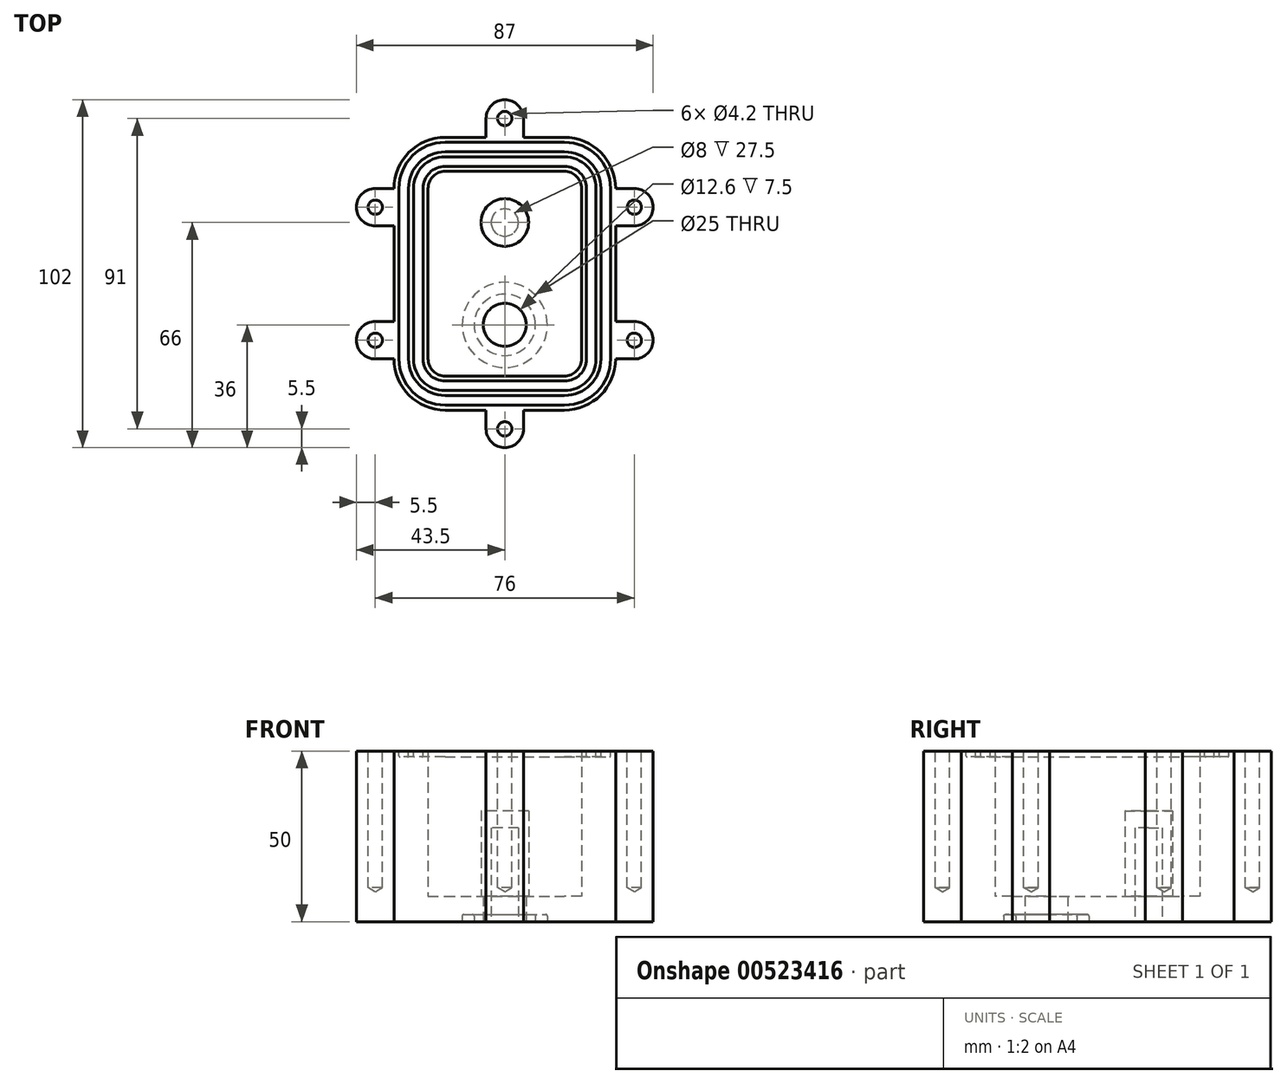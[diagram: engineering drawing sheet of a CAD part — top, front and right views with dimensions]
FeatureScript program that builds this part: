
annotation { "Feature Type Name" : "Feature", "Feature Type Description" : "" }
export const myFeature = defineFeature(function(context is Context, id is Id, definition is map)
    precondition{}
    {
        {
            var Q0;
            Q0=qCreatedBy(makeId("Top.planeOp"),FACE);
            var sketch = newSketch(context, id + "F0", { "sketchPlane" : qUnion([Q0])});
            skLineSegment(sketch, "E0.bottom", {"start": v(-17.5, -30) * mm, "end": v(17.5, -30) * mm});
            skLineSegment(sketch, "E0.top", {"start": v(-17.5, 30) * mm, "end": v(17.5, 30) * mm});
            skLineSegment(sketch, "E0.left", {"start": v(-22.5, -25) * mm, "end": v(-22.5, 25) * mm});
            skLineSegment(sketch, "E0.right", {"start": v(22.5, -25) * mm, "end": v(22.5, 25) * mm});
            skPoint(sketch, "E0.middle", {"position": v(0, 0) * mm});
            skPoint(sketch, "E1.visualSharp", {"position": v(22.5, -30) * mm});
            skArc(sketch, "E1.filletArc", {"start": v(17.5, -30) * mm, "mid": v(21.04, -28.54) * mm, "end": v(22.5, -25) * mm});
            skPoint(sketch, "E2.visualSharp", {"position": v(-22.5, -30) * mm});
            skArc(sketch, "E2.filletArc", {"start": v(-22.5, -25) * mm, "mid": v(-21.04, -28.54) * mm, "end": v(-17.5, -30) * mm});
            skPoint(sketch, "E3.visualSharp", {"position": v(-22.5, 30) * mm});
            skArc(sketch, "E3.filletArc", {"start": v(-17.5, 30) * mm, "mid": v(-21.04, 28.54) * mm, "end": v(-22.5, 25) * mm});
            skPoint(sketch, "E4.visualSharp", {"position": v(22.5, 30) * mm});
            skArc(sketch, "E4.filletArc", {"start": v(22.5, 25) * mm, "mid": v(21.04, 28.54) * mm, "end": v(17.5, 30) * mm});
            skArc(sketch, "E5.0", {"start": v(-32.5, -25) * mm, "mid": v(-28.1, -35.6) * mm, "end": v(-17.5, -40) * mm});
            skLineSegment(sketch, "E5.1", {"start": v(-17.5, -40) * mm, "end": v(-5.5, -40) * mm});
            skLineSegment(sketch, "E5.2", {"start": v(-32.5, -14) * mm, "end": v(-32.5, 14) * mm});
            skArc(sketch, "E5.3", {"start": v(17.5, -40) * mm, "mid": v(28.1, -35.6) * mm, "end": v(32.5, -25) * mm});
            skArc(sketch, "E5.4", {"start": v(-17.5, 40) * mm, "mid": v(-28.1, 35.6) * mm, "end": v(-32.5, 25) * mm});
            skLineSegment(sketch, "E5.5", {"start": v(-17.5, 40) * mm, "end": v(-5.5, 40) * mm});
            skArc(sketch, "E5.6", {"start": v(32.5, 25) * mm, "mid": v(28.1, 35.6) * mm, "end": v(17.5, 40) * mm});
            skLineSegment(sketch, "E5.7", {"start": v(32.5, -14) * mm, "end": v(32.5, 14) * mm});
            skArc(sketch, "E6", {"start": v(-38, 25) * mm, "mid": v(-43.5, 19.5) * mm, "end": v(-38, 14) * mm});
            skLineSegment(sketch, "E7", {"start": v(-38, 25) * mm, "end": v(-32.5, 25) * mm});
            skLineSegment(sketch, "E8", {"start": v(-38, 14) * mm, "end": v(-32.5, 14) * mm});
            skCircle(sketch, "E9", {"center": v(-38, 19.5) * mm, "radius": 2.5 * mm, "construction": true});
            skLineSegment(sketch, "E10", {"start": v(0, 49.94) * mm, "end": v(0, -61.1) * mm, "construction": true});
            skLineSegment(sketch, "E11", {"start": v(-88.08, 0) * mm, "end": v(87.86, 0) * mm, "construction": true});
            skLineSegment(sketch, "E12.MirrorCS", {"start": v(38, 25) * mm, "end": v(32.5, 25) * mm});
            skLineSegment(sketch, "E13.MirrorCS", {"start": v(38, 14) * mm, "end": v(32.5, 14) * mm});
            skArc(sketch, "E14.MirrorCS", {"start": v(38, 25) * mm, "mid": v(43.5, 19.5) * mm, "end": v(38, 14) * mm});
            skCircle(sketch, "E15.MirrorC", {"center": v(38, 19.5) * mm, "radius": 2.5 * mm, "construction": true});
            skLineSegment(sketch, "E16.MirrorCS", {"start": v(-38, -14) * mm, "end": v(-32.5, -14) * mm});
            skLineSegment(sketch, "E17.MirrorCS", {"start": v(-38, -25) * mm, "end": v(-32.5, -25) * mm});
            skArc(sketch, "E18.MirrorCS", {"start": v(-38, -25) * mm, "mid": v(-43.5, -19.5) * mm, "end": v(-38, -14) * mm});
            skCircle(sketch, "E19.MirrorC", {"center": v(-38, -19.5) * mm, "radius": 2.5 * mm, "construction": true});
            skArc(sketch, "E20.MirrorCS", {"start": v(32.5, -25) * mm, "mid": v(28.1, -35.6) * mm, "end": v(17.5, -40) * mm});
            skLineSegment(sketch, "E21.MirrorCS", {"start": v(38, -14) * mm, "end": v(32.5, -14) * mm});
            skArc(sketch, "E22.MirrorCS", {"start": v(38, -25) * mm, "mid": v(43.5, -19.5) * mm, "end": v(38, -14) * mm});
            skLineSegment(sketch, "E23.MirrorCS", {"start": v(32.5, 14) * mm, "end": v(32.5, -14) * mm});
            skCircle(sketch, "E24.MirrorC", {"center": v(38, -19.5) * mm, "radius": 2.5 * mm, "construction": true});
            skLineSegment(sketch, "E25.MirrorCS", {"start": v(38, -25) * mm, "end": v(32.5, -25) * mm});
            skPoint(sketch, "E26.orphan", {"position": v(32.5, 25) * mm});
            skArc(sketch, "E27", {"start": v(5.5, 45.5) * mm, "mid": v(0, 51) * mm, "end": v(-5.5, 45.5) * mm});
            skCircle(sketch, "E28", {"center": v(0, 45.5) * mm, "radius": 2.5 * mm, "construction": true});
            skLineSegment(sketch, "E29", {"start": v(5.5, 45.5) * mm, "end": v(5.5, 40) * mm});
            skLineSegment(sketch, "E30", {"start": v(-5.5, 45.5) * mm, "end": v(-5.5, 40) * mm});
            skLineSegment(sketch, "E31.trimOffspring", {"start": v(5.5, 40) * mm, "end": v(17.5, 40) * mm});
            skArc(sketch, "E32.MirrorCS", {"start": v(5.5, -45.5) * mm, "mid": v(0, -51) * mm, "end": v(-5.5, -45.5) * mm});
            skCircle(sketch, "E33.MirrorC", {"center": v(0, -45.5) * mm, "radius": 2.5 * mm, "construction": true});
            skLineSegment(sketch, "E34.MirrorCS", {"start": v(5.5, -45.5) * mm, "end": v(5.5, -40) * mm});
            skLineSegment(sketch, "E35.MirrorCS", {"start": v(-5.5, -45.5) * mm, "end": v(-5.5, -40) * mm});
            skLineSegment(sketch, "E36.trimOffspring", {"start": v(5.5, -40) * mm, "end": v(17.5, -40) * mm});
            skSolve(sketch);
        }
        {
            var Q0;
            Q0=qSketchRegion(id+"F0",true);
            extrude(context, id + "F1", {"entities" : qUnion([Q0]), "depth" : 50 * mm, "offsetDistance" : 25 * mm});
        }
        {
            var Q0;
            Q0=qCreatedBy(makeId("Top.planeOp"),FACE);
            var sketch = newSketch(context, id + "F2", { "sketchPlane" : qUnion([Q0])});
            skArc(sketch, "E37.0.0", {"start": v(38, 25) * mm, "mid": v(43.5, 19.5) * mm, "end": v(38, 14) * mm});
            skLineSegment(sketch, "E37.0.1", {"start": v(38, 14) * mm, "end": v(32.5, 14) * mm});
            skLineSegment(sketch, "E37.0.2", {"start": v(32.5, 14) * mm, "end": v(32.5, -14) * mm});
            skLineSegment(sketch, "E37.0.3", {"start": v(32.5, -14) * mm, "end": v(38, -14) * mm});
            skArc(sketch, "E37.0.4", {"start": v(38, -14) * mm, "mid": v(43.5, -19.5) * mm, "end": v(38, -25) * mm});
            skLineSegment(sketch, "E37.0.5", {"start": v(38, -25) * mm, "end": v(32.5, -25) * mm});
            skArc(sketch, "E37.0.6", {"start": v(32.5, -25) * mm, "mid": v(28.1, -35.6) * mm, "end": v(17.5, -40) * mm});
            skLineSegment(sketch, "E37.0.7", {"start": v(17.5, -40) * mm, "end": v(5.5, -40) * mm});
            skLineSegment(sketch, "E37.0.8", {"start": v(5.5, -40) * mm, "end": v(5.5, -45.5) * mm});
            skArc(sketch, "E37.0.9", {"start": v(5.5, -45.5) * mm, "mid": v(0, -51) * mm, "end": v(-5.5, -45.5) * mm});
            skLineSegment(sketch, "E37.0.10", {"start": v(-5.5, -45.5) * mm, "end": v(-5.5, -40) * mm});
            skLineSegment(sketch, "E37.0.11", {"start": v(-5.5, -40) * mm, "end": v(-17.5, -40) * mm});
            skArc(sketch, "E37.0.12", {"start": v(-17.5, -40) * mm, "mid": v(-28.1, -35.6) * mm, "end": v(-32.5, -25) * mm});
            skLineSegment(sketch, "E37.0.13", {"start": v(-32.5, -25) * mm, "end": v(-38, -25) * mm});
            skArc(sketch, "E37.0.14", {"start": v(-38, -25) * mm, "mid": v(-43.5, -19.5) * mm, "end": v(-38, -14) * mm});
            skLineSegment(sketch, "E37.0.15", {"start": v(-38, -14) * mm, "end": v(-32.5, -14) * mm});
            skLineSegment(sketch, "E37.0.16", {"start": v(-32.5, -14) * mm, "end": v(-32.5, 14) * mm});
            skLineSegment(sketch, "E37.0.17", {"start": v(-32.5, 14) * mm, "end": v(-38, 14) * mm});
            skArc(sketch, "E37.0.18", {"start": v(-38, 14) * mm, "mid": v(-43.5, 19.5) * mm, "end": v(-38, 25) * mm});
            skLineSegment(sketch, "E37.0.19", {"start": v(-38, 25) * mm, "end": v(-32.5, 25) * mm});
            skArc(sketch, "E37.0.20", {"start": v(-32.5, 25) * mm, "mid": v(-28.1, 35.6) * mm, "end": v(-17.5, 40) * mm});
            skLineSegment(sketch, "E37.0.21", {"start": v(-17.5, 40) * mm, "end": v(-5.5, 40) * mm});
            skLineSegment(sketch, "E37.0.22", {"start": v(-5.5, 40) * mm, "end": v(-5.5, 45.5) * mm});
            skArc(sketch, "E37.0.23", {"start": v(-5.5, 45.5) * mm, "mid": v(0, 51) * mm, "end": v(5.5, 45.5) * mm});
            skLineSegment(sketch, "E37.0.24", {"start": v(5.5, 45.5) * mm, "end": v(5.5, 40) * mm});
            skLineSegment(sketch, "E37.0.25", {"start": v(5.5, 40) * mm, "end": v(17.5, 40) * mm});
            skArc(sketch, "E37.0.26", {"start": v(17.5, 40) * mm, "mid": v(28.1, 35.6) * mm, "end": v(32.5, 25) * mm});
            skLineSegment(sketch, "E37.0.27", {"start": v(32.5, 25) * mm, "end": v(38, 25) * mm});
            skSolve(sketch);
        }
        {
            var Q0;
            Q0=qSketchRegion(id+"F2",true);
            var Q1;
            Q1=qSketchRegion(id+"F0",true);
            extrude(context, id + "F3", {"entities" : qUnion([Q0, Q1]), "operationType" : NewBodyOperationType.ADD, "depth" : 7.5 * mm, "offsetDistance" : 25 * mm});
        }
        {
            var Q0;
            Q0=makeQuery(id+"F1.opExtrude","CAP_FACE",FACE,{"disambiguationData":[OSD([sQuery(id+"F0.wireOp",EDGE,"E0.bottom"),sQuery(id+"F0.wireOp",EDGE,"E0.top"),sQuery(id+"F0.wireOp",EDGE,"E0.left"),sQuery(id+"F0.wireOp",EDGE,"E0.right"),sQuery(id+"F0.wireOp",EDGE,"E1.filletArc"),sQuery(id+"F0.wireOp",EDGE,"E2.filletArc"),sQuery(id+"F0.wireOp",EDGE,"E3.filletArc"),sQuery(id+"F0.wireOp",EDGE,"E4.filletArc"),sQuery(id+"F0.wireOp",EDGE,"E5.0"),sQuery(id+"F0.wireOp",EDGE,"E5.1"),sQuery(id+"F0.wireOp",EDGE,"E5.2"),sQuery(id+"F0.wireOp",EDGE,"E5.3"),sQuery(id+"F0.wireOp",EDGE,"E5.4"),sQuery(id+"F0.wireOp",EDGE,"E5.5"),sQuery(id+"F0.wireOp",EDGE,"E5.6"),sQuery(id+"F0.wireOp",EDGE,"E5.7")])],"isStart":false});
            var sketch = newSketch(context, id + "F4", { "sketchPlane" : qUnion([Q0])});
            skLineSegment(sketch, "E38.0", {"start": v(-17.5, 31.47) * mm, "end": v(17.5, 31.47) * mm});
            skArc(sketch, "E38.1", {"start": v(23.97, 25) * mm, "mid": v(22.07, 29.57) * mm, "end": v(17.5, 31.47) * mm});
            skArc(sketch, "E38.2", {"start": v(-17.5, 31.47) * mm, "mid": v(-22.07, 29.57) * mm, "end": v(-23.97, 25) * mm});
            skLineSegment(sketch, "E38.3", {"start": v(23.97, -25) * mm, "end": v(23.97, 25) * mm});
            skLineSegment(sketch, "E38.4", {"start": v(-23.97, -25) * mm, "end": v(-23.97, 25) * mm});
            skArc(sketch, "E38.5", {"start": v(-23.97, -25) * mm, "mid": v(-22.07, -29.57) * mm, "end": v(-17.5, -31.47) * mm});
            skLineSegment(sketch, "E38.6", {"start": v(-17.5, -31.47) * mm, "end": v(17.5, -31.47) * mm});
            skArc(sketch, "E38.7", {"start": v(17.5, -31.47) * mm, "mid": v(22.07, -29.57) * mm, "end": v(23.97, -25) * mm});
            skLineSegment(sketch, "E39.0", {"start": v(-17.5, 34.27) * mm, "end": v(17.5, 34.27) * mm});
            skArc(sketch, "E39.1", {"start": v(26.77, 25) * mm, "mid": v(24.05, 31.55) * mm, "end": v(17.5, 34.27) * mm});
            skArc(sketch, "E39.2", {"start": v(-17.5, 34.27) * mm, "mid": v(-24.05, 31.55) * mm, "end": v(-26.77, 25) * mm});
            skLineSegment(sketch, "E39.3", {"start": v(26.77, -25) * mm, "end": v(26.77, 25) * mm});
            skLineSegment(sketch, "E39.4", {"start": v(-26.77, -25) * mm, "end": v(-26.77, 25) * mm});
            skArc(sketch, "E39.5", {"start": v(-26.77, -25) * mm, "mid": v(-24.05, -31.55) * mm, "end": v(-17.5, -34.27) * mm});
            skLineSegment(sketch, "E39.6", {"start": v(-17.5, -34.27) * mm, "end": v(17.5, -34.27) * mm});
            skArc(sketch, "E39.7", {"start": v(17.5, -34.27) * mm, "mid": v(24.05, -31.55) * mm, "end": v(26.77, -25) * mm});
            skLineSegment(sketch, "E40.0", {"start": v(-17.5, 35.73) * mm, "end": v(17.5, 35.73) * mm});
            skArc(sketch, "E40.1", {"start": v(28.23, 25) * mm, "mid": v(25.09, 32.59) * mm, "end": v(17.5, 35.73) * mm});
            skArc(sketch, "E40.2", {"start": v(-17.5, 35.73) * mm, "mid": v(-25.09, 32.59) * mm, "end": v(-28.23, 25) * mm});
            skLineSegment(sketch, "E40.3", {"start": v(28.23, -25) * mm, "end": v(28.23, 25) * mm});
            skLineSegment(sketch, "E40.4", {"start": v(-28.23, -25) * mm, "end": v(-28.23, 25) * mm});
            skArc(sketch, "E40.5", {"start": v(-28.23, -25) * mm, "mid": v(-25.09, -32.59) * mm, "end": v(-17.5, -35.73) * mm});
            skLineSegment(sketch, "E40.6", {"start": v(-17.5, -35.73) * mm, "end": v(17.5, -35.73) * mm});
            skArc(sketch, "E40.7", {"start": v(17.5, -35.73) * mm, "mid": v(25.09, -32.59) * mm, "end": v(28.23, -25) * mm});
            skLineSegment(sketch, "E41.0", {"start": v(-17.5, 38.53) * mm, "end": v(17.5, 38.53) * mm});
            skArc(sketch, "E41.1", {"start": v(31.03, 25) * mm, "mid": v(27.07, 34.57) * mm, "end": v(17.5, 38.53) * mm});
            skArc(sketch, "E41.2", {"start": v(-17.5, 38.53) * mm, "mid": v(-27.07, 34.57) * mm, "end": v(-31.03, 25) * mm});
            skLineSegment(sketch, "E41.3", {"start": v(31.03, -25) * mm, "end": v(31.03, 25) * mm});
            skLineSegment(sketch, "E41.4", {"start": v(-31.03, -25) * mm, "end": v(-31.03, 25) * mm});
            skArc(sketch, "E41.5", {"start": v(-31.03, -25) * mm, "mid": v(-27.07, -34.57) * mm, "end": v(-17.5, -38.53) * mm});
            skLineSegment(sketch, "E41.6", {"start": v(-17.5, -38.53) * mm, "end": v(17.5, -38.53) * mm});
            skArc(sketch, "E41.7", {"start": v(17.5, -38.53) * mm, "mid": v(27.07, -34.57) * mm, "end": v(31.03, -25) * mm});
            skLineSegment(sketch, "E42", {"start": v(0, 30) * mm, "end": v(0, 31.47) * mm, "construction": true});
            skLineSegment(sketch, "E43", {"start": v(0, 31.47) * mm, "end": v(0, 34.27) * mm, "construction": true});
            skLineSegment(sketch, "E44", {"start": v(0, 34.27) * mm, "end": v(0, 35.73) * mm, "construction": true});
            skLineSegment(sketch, "E45", {"start": v(0, 35.73) * mm, "end": v(0, 38.53) * mm, "construction": true});
            skLineSegment(sketch, "E46", {"start": v(0, 38.53) * mm, "end": v(0, 40) * mm, "construction": true});
            skSolve(sketch);
        }
        {
            var Q0;
            Q0=makeQuery(id+"F4.imprint","IMPRINT",FACE,{"disambiguationData":[TD([[makeQuery(id+"F4.imprint","IMPRINT",EDGE,{"derivedFrom":sQuery(id+"F4.wireOp",EDGE,"E40.0")}),1.0]])]});
            var Q1;
            Q1=makeQuery(id+"F4.imprint","IMPRINT",FACE,{"disambiguationData":[TD([[makeQuery(id+"F4.imprint","IMPRINT",EDGE,{"derivedFrom":sQuery(id+"F4.wireOp",EDGE,"E38.0")}),1.0]])]});
            extrude(context, id + "F5", {"entities" : qUnion([Q0, Q1]), "operationType" : NewBodyOperationType.REMOVE, "oppositeDirection" : true, "depth" : 1.7 * mm, "offsetDistance" : 25 * mm});
        }
        {
            var Q0;
            {var subQ0=sQuery(id+"F0.wireOp",EDGE,"E25.MirrorCS");var subQ1=sQuery(id+"F0.wireOp",EDGE,"E23.MirrorCS");var subQ2=sQuery(id+"F0.wireOp",EDGE,"E22.MirrorCS");var subQ3=sQuery(id+"F0.wireOp",EDGE,"E21.MirrorCS");var subQ4=sQuery(id+"F0.wireOp",EDGE,"E20.MirrorCS");var subQ5=sQuery(id+"F0.wireOp",EDGE,"E18.MirrorCS");var subQ6=sQuery(id+"F0.wireOp",EDGE,"E17.MirrorCS");var subQ7=sQuery(id+"F0.wireOp",EDGE,"E16.MirrorCS");var subQ8=sQuery(id+"F0.wireOp",EDGE,"E14.MirrorCS");var subQ9=sQuery(id+"F0.wireOp",EDGE,"E13.MirrorCS");var subQ10=sQuery(id+"F0.wireOp",EDGE,"E5.4");var subQ11=sQuery(id+"F0.wireOp",EDGE,"E5.2");var subQ12=sQuery(id+"F0.wireOp",EDGE,"E5.1");var subQ13=sQuery(id+"F0.wireOp",EDGE,"E5.0");var subQ14=sQuery(id+"F0.wireOp",EDGE,"E5.5");var subQ15=sQuery(id+"F0.wireOp",EDGE,"E5.6");var subQ16=sQuery(id+"F0.wireOp",EDGE,"E6");var subQ17=sQuery(id+"F0.wireOp",EDGE,"E7");var subQ18=sQuery(id+"F0.wireOp",EDGE,"E8");var subQ19=sQuery(id+"F0.wireOp",EDGE,"E12.MirrorCS");Q0=makeQuery(id+"F5.boolean.opBoolean","SPLIT",FACE,{"disambiguationData":[TD([makeQuery(id+"F1.opExtrude","SWEPT_FACE",FACE,{"disambiguationData":[OSD([subQ13])]})])],"derivedFrom":makeQuery(id+"F1.opExtrude","CAP_FACE",FACE,{"disambiguationData":[OSD([sQuery(id+"F0.wireOp",EDGE,"E0.bottom"),sQuery(id+"F0.wireOp",EDGE,"E0.top"),sQuery(id+"F0.wireOp",EDGE,"E0.left"),sQuery(id+"F0.wireOp",EDGE,"E0.right"),sQuery(id+"F0.wireOp",EDGE,"E1.filletArc"),sQuery(id+"F0.wireOp",EDGE,"E2.filletArc"),sQuery(id+"F0.wireOp",EDGE,"E3.filletArc"),sQuery(id+"F0.wireOp",EDGE,"E4.filletArc"),subQ13,subQ12,subQ11,subQ10,subQ14,subQ15,subQ16,subQ17,subQ18,subQ19,subQ9,subQ8,subQ7,subQ6,subQ5,subQ4,subQ3,subQ2,subQ1,subQ0])],"isStart":false})});}
            var sketch = newSketch(context, id + "F6", { "sketchPlane" : qUnion([Q0])});
            skPoint(sketch, "E47", {"position": v(-38, 19.5) * mm});
            skPoint(sketch, "E48", {"position": v(0, 45.5) * mm});
            skPoint(sketch, "E49", {"position": v(38, 19.5) * mm});
            skPoint(sketch, "E50", {"position": v(38, -19.5) * mm});
            skPoint(sketch, "E51", {"position": v(0, -45.5) * mm});
            skPoint(sketch, "E52", {"position": v(-38, -19.5) * mm});
            skSolve(sketch);
        }
        {
            var Q0;
            Q0=sQuery(id+"F6.wireOp",VERTEX,"E47");
            var Q1;
            Q1=sQuery(id+"F6.wireOp",VERTEX,"E48");
            var Q2;
            Q2=sQuery(id+"F6.wireOp",VERTEX,"E49");
            var Q3;
            Q3=sQuery(id+"F6.wireOp",VERTEX,"E50");
            var Q4;
            Q4=sQuery(id+"F6.wireOp",VERTEX,"E51");
            var Q5;
            Q5=sQuery(id+"F6.wireOp",VERTEX,"E52");
            var Q6;
            Q6=makeQuery(id+"F1.opExtrude","SWEPT_BODY",BODY,{"disambiguationData":[OSD([sQuery(id+"F0.wireOp",EDGE,"E0.bottom"),sQuery(id+"F0.wireOp",EDGE,"E0.top"),sQuery(id+"F0.wireOp",EDGE,"E0.left"),sQuery(id+"F0.wireOp",EDGE,"E0.right"),sQuery(id+"F0.wireOp",EDGE,"E1.filletArc"),sQuery(id+"F0.wireOp",EDGE,"E2.filletArc"),sQuery(id+"F0.wireOp",EDGE,"E3.filletArc"),sQuery(id+"F0.wireOp",EDGE,"E4.filletArc"),sQuery(id+"F0.wireOp",EDGE,"E5.0"),sQuery(id+"F0.wireOp",EDGE,"E5.1"),sQuery(id+"F0.wireOp",EDGE,"E5.2"),sQuery(id+"F0.wireOp",EDGE,"E5.4"),sQuery(id+"F0.wireOp",EDGE,"E5.5"),sQuery(id+"F0.wireOp",EDGE,"E5.6"),sQuery(id+"F0.wireOp",EDGE,"E6"),sQuery(id+"F0.wireOp",EDGE,"E7"),sQuery(id+"F0.wireOp",EDGE,"E8"),sQuery(id+"F0.wireOp",EDGE,"E12.MirrorCS"),sQuery(id+"F0.wireOp",EDGE,"E13.MirrorCS"),sQuery(id+"F0.wireOp",EDGE,"E14.MirrorCS"),sQuery(id+"F0.wireOp",EDGE,"E16.MirrorCS"),sQuery(id+"F0.wireOp",EDGE,"E17.MirrorCS"),sQuery(id+"F0.wireOp",EDGE,"E18.MirrorCS"),sQuery(id+"F0.wireOp",EDGE,"E20.MirrorCS"),sQuery(id+"F0.wireOp",EDGE,"E21.MirrorCS"),sQuery(id+"F0.wireOp",EDGE,"E22.MirrorCS"),sQuery(id+"F0.wireOp",EDGE,"E23.MirrorCS"),sQuery(id+"F0.wireOp",EDGE,"E25.MirrorCS"),sQuery(id+"F0.wireOp",EDGE,"E27"),sQuery(id+"F0.wireOp",EDGE,"E29"),sQuery(id+"F0.wireOp",EDGE,"E30"),sQuery(id+"F0.wireOp",EDGE,"E31.trimOffspring"),sQuery(id+"F0.wireOp",EDGE,"E32.MirrorCS"),sQuery(id+"F0.wireOp",EDGE,"E34.MirrorCS"),sQuery(id+"F0.wireOp",EDGE,"E35.MirrorCS"),sQuery(id+"F0.wireOp",EDGE,"E36.trimOffspring")])]});
            hole(context, id + "F7", {"style" : HoleStyle.SIMPLE, "endStyle" : HoleEndStyle.BLIND, "standardTappedOrClearance" : lookupTablePath({ "standard" : "ISO", "engagement" : "75%", "pitch" : "0.8 mm", "size" : "M5", "type" : "Tapped" }), "standardBlindInLast" : lookupTablePath({ "standard" : "ISO", "engagement" : "75%", "pitch" : "0.8 mm", "size" : "M5", "type" : "Tapped" }), "holeDiameter" : 4.2 * mm, "showTappedDepth" : true, "holeDepth" : 40 * mm, "isTappedThrough" : true, "tappedDepth" : 37.6 * mm, "tapClearance" : 3, "locations" : qUnion([Q0, Q1, Q2, Q3, Q4, Q5]), "scope" : qUnion([Q6]), "majorDiameter" : 5 * mm});
        }
        {
            var Q0;
            Q0=makeQuery(id+"F5.boolean.opBoolean","COPY",FACE,{"derivedFrom":makeQuery(id+"F5.opExtrude","CAP_FACE",FACE,{"disambiguationData":[OSD([sQuery(id+"F4.wireOp",EDGE,"E40.0"),sQuery(id+"F4.wireOp",EDGE,"E40.1"),sQuery(id+"F4.wireOp",EDGE,"E40.2"),sQuery(id+"F4.wireOp",EDGE,"E40.3"),sQuery(id+"F4.wireOp",EDGE,"E40.4"),sQuery(id+"F4.wireOp",EDGE,"E40.5"),sQuery(id+"F4.wireOp",EDGE,"E40.6"),sQuery(id+"F4.wireOp",EDGE,"E40.7"),sQuery(id+"F4.wireOp",EDGE,"E41.0"),sQuery(id+"F4.wireOp",EDGE,"E41.1"),sQuery(id+"F4.wireOp",EDGE,"E41.2"),sQuery(id+"F4.wireOp",EDGE,"E41.3"),sQuery(id+"F4.wireOp",EDGE,"E41.4"),sQuery(id+"F4.wireOp",EDGE,"E41.5"),sQuery(id+"F4.wireOp",EDGE,"E41.6"),sQuery(id+"F4.wireOp",EDGE,"E41.7")])],"isStart":false})});
            var Q1;
            Q1=makeQuery(id+"F5.boolean.opBoolean","COPY",FACE,{"derivedFrom":makeQuery(id+"F5.opExtrude","CAP_FACE",FACE,{"disambiguationData":[OSD([sQuery(id+"F4.wireOp",EDGE,"E38.0"),sQuery(id+"F4.wireOp",EDGE,"E38.1"),sQuery(id+"F4.wireOp",EDGE,"E38.2"),sQuery(id+"F4.wireOp",EDGE,"E38.3"),sQuery(id+"F4.wireOp",EDGE,"E38.4"),sQuery(id+"F4.wireOp",EDGE,"E38.5"),sQuery(id+"F4.wireOp",EDGE,"E38.6"),sQuery(id+"F4.wireOp",EDGE,"E38.7"),sQuery(id+"F4.wireOp",EDGE,"E39.0"),sQuery(id+"F4.wireOp",EDGE,"E39.1"),sQuery(id+"F4.wireOp",EDGE,"E39.2"),sQuery(id+"F4.wireOp",EDGE,"E39.3"),sQuery(id+"F4.wireOp",EDGE,"E39.4"),sQuery(id+"F4.wireOp",EDGE,"E39.5"),sQuery(id+"F4.wireOp",EDGE,"E39.6"),sQuery(id+"F4.wireOp",EDGE,"E39.7")])],"isStart":false})});
            fillet(context, id + "F8", {"entities" : qUnion([Q0, Q1]), "radius" : 0.3 * mm, "tangentPropagation" : true, "allowEdgeOverflow" : false});
        }
        {
            var Q0;
            Q0=makeQuery(id+"F3.boolean.opBoolean","MERGE",FACE,{"derivedFrom":[makeQuery(id+"F3.opExtrude","CAP_FACE",FACE,{"disambiguationData":[OSD([sQuery(id+"F0.wireOp",EDGE,"E0.bottom"),sQuery(id+"F0.wireOp",EDGE,"E0.top"),sQuery(id+"F0.wireOp",EDGE,"E0.left"),sQuery(id+"F0.wireOp",EDGE,"E0.right"),sQuery(id+"F0.wireOp",EDGE,"E1.filletArc"),sQuery(id+"F0.wireOp",EDGE,"E2.filletArc"),sQuery(id+"F0.wireOp",EDGE,"E3.filletArc"),sQuery(id+"F0.wireOp",EDGE,"E4.filletArc"),sQuery(id+"F0.wireOp",EDGE,"E5.0"),sQuery(id+"F0.wireOp",EDGE,"E5.1"),sQuery(id+"F0.wireOp",EDGE,"E5.2"),sQuery(id+"F0.wireOp",EDGE,"E5.4"),sQuery(id+"F0.wireOp",EDGE,"E5.5"),sQuery(id+"F0.wireOp",EDGE,"E5.6"),sQuery(id+"F0.wireOp",EDGE,"E6"),sQuery(id+"F0.wireOp",EDGE,"E7"),sQuery(id+"F0.wireOp",EDGE,"E8"),sQuery(id+"F0.wireOp",EDGE,"E12.MirrorCS"),sQuery(id+"F0.wireOp",EDGE,"E13.MirrorCS"),sQuery(id+"F0.wireOp",EDGE,"E14.MirrorCS"),sQuery(id+"F0.wireOp",EDGE,"E16.MirrorCS"),sQuery(id+"F0.wireOp",EDGE,"E17.MirrorCS"),sQuery(id+"F0.wireOp",EDGE,"E18.MirrorCS"),sQuery(id+"F0.wireOp",EDGE,"E20.MirrorCS"),sQuery(id+"F0.wireOp",EDGE,"E21.MirrorCS"),sQuery(id+"F0.wireOp",EDGE,"E22.MirrorCS"),sQuery(id+"F0.wireOp",EDGE,"E23.MirrorCS"),sQuery(id+"F0.wireOp",EDGE,"E25.MirrorCS"),sQuery(id+"F0.wireOp",EDGE,"E27"),sQuery(id+"F0.wireOp",EDGE,"E29"),sQuery(id+"F0.wireOp",EDGE,"E30"),sQuery(id+"F0.wireOp",EDGE,"E31.trimOffspring"),sQuery(id+"F0.wireOp",EDGE,"E32.MirrorCS"),sQuery(id+"F0.wireOp",EDGE,"E34.MirrorCS"),sQuery(id+"F0.wireOp",EDGE,"E35.MirrorCS"),sQuery(id+"F0.wireOp",EDGE,"E36.trimOffspring")])],"isStart":false}),makeQuery(id+"F3.opExtrude","CAP_FACE",FACE,{"disambiguationData":[OSD([sQuery(id+"F2.wireOp",EDGE,"E37.0.0"),sQuery(id+"F2.wireOp",EDGE,"E37.0.1"),sQuery(id+"F2.wireOp",EDGE,"E37.0.2"),sQuery(id+"F2.wireOp",EDGE,"E37.0.3"),sQuery(id+"F2.wireOp",EDGE,"E37.0.4"),sQuery(id+"F2.wireOp",EDGE,"E37.0.5"),sQuery(id+"F2.wireOp",EDGE,"E37.0.6"),sQuery(id+"F2.wireOp",EDGE,"E37.0.7"),sQuery(id+"F2.wireOp",EDGE,"E37.0.8"),sQuery(id+"F2.wireOp",EDGE,"E37.0.9"),sQuery(id+"F2.wireOp",EDGE,"E37.0.10"),sQuery(id+"F2.wireOp",EDGE,"E37.0.11"),sQuery(id+"F2.wireOp",EDGE,"E37.0.12"),sQuery(id+"F2.wireOp",EDGE,"E37.0.13"),sQuery(id+"F2.wireOp",EDGE,"E37.0.14"),sQuery(id+"F2.wireOp",EDGE,"E37.0.15"),sQuery(id+"F2.wireOp",EDGE,"E37.0.16"),sQuery(id+"F2.wireOp",EDGE,"E37.0.17"),sQuery(id+"F2.wireOp",EDGE,"E37.0.18"),sQuery(id+"F2.wireOp",EDGE,"E37.0.19"),sQuery(id+"F2.wireOp",EDGE,"E37.0.20"),sQuery(id+"F2.wireOp",EDGE,"E37.0.21"),sQuery(id+"F2.wireOp",EDGE,"E37.0.22"),sQuery(id+"F2.wireOp",EDGE,"E37.0.23"),sQuery(id+"F2.wireOp",EDGE,"E37.0.24"),sQuery(id+"F2.wireOp",EDGE,"E37.0.25"),sQuery(id+"F2.wireOp",EDGE,"E37.0.26"),sQuery(id+"F2.wireOp",EDGE,"E37.0.27")])],"isStart":false})]});
            var sketch = newSketch(context, id + "F9", { "sketchPlane" : qUnion([Q0])});
            skCircle(sketch, "E53", {"center": v(0, 15) * mm, "radius": 7 * mm});
            skLineSegment(sketch, "E54", {"start": v(0, 0) * mm, "end": v(0, 15) * mm, "construction": true});
            skLineSegment(sketch, "E55", {"start": v(0, 15) * mm, "end": v(0, 30) * mm, "construction": true});
            skSolve(sketch);
        }
        {
            var Q0;
            Q0 = qSketchRegion(id + "F9", true);
            extrude(context, id + "F10", {"entities" : qUnion([Q0]), "operationType" : NewBodyOperationType.ADD, "depth" : 25 * mm, "offsetDistance" : 25 * mm});
        }
        {
            var Q0;
            {var subQ0=sQuery(id+"F0.wireOp",EDGE,"E36.trimOffspring");var subQ1=sQuery(id+"F0.wireOp",EDGE,"E35.MirrorCS");var subQ2=sQuery(id+"F0.wireOp",EDGE,"E34.MirrorCS");var subQ3=sQuery(id+"F0.wireOp",EDGE,"E32.MirrorCS");var subQ4=sQuery(id+"F0.wireOp",EDGE,"E31.trimOffspring");var subQ5=sQuery(id+"F0.wireOp",EDGE,"E30");var subQ6=sQuery(id+"F0.wireOp",EDGE,"E29");var subQ7=sQuery(id+"F0.wireOp",EDGE,"E27");var subQ8=sQuery(id+"F0.wireOp",EDGE,"E25.MirrorCS");var subQ9=sQuery(id+"F0.wireOp",EDGE,"E23.MirrorCS");var subQ10=sQuery(id+"F0.wireOp",EDGE,"E22.MirrorCS");var subQ11=sQuery(id+"F0.wireOp",EDGE,"E21.MirrorCS");var subQ12=sQuery(id+"F0.wireOp",EDGE,"E20.MirrorCS");var subQ13=sQuery(id+"F0.wireOp",EDGE,"E18.MirrorCS");var subQ14=sQuery(id+"F0.wireOp",EDGE,"E17.MirrorCS");var subQ15=sQuery(id+"F0.wireOp",EDGE,"E16.MirrorCS");var subQ16=sQuery(id+"F0.wireOp",EDGE,"E14.MirrorCS");var subQ17=sQuery(id+"F0.wireOp",EDGE,"E13.MirrorCS");var subQ18=sQuery(id+"F0.wireOp",EDGE,"E12.MirrorCS");var subQ19=sQuery(id+"F0.wireOp",EDGE,"E8");var subQ20=sQuery(id+"F0.wireOp",EDGE,"E7");var subQ21=sQuery(id+"F0.wireOp",EDGE,"E6");var subQ22=sQuery(id+"F0.wireOp",EDGE,"E5.6");var subQ23=sQuery(id+"F0.wireOp",EDGE,"E5.5");var subQ24=sQuery(id+"F0.wireOp",EDGE,"E5.4");var subQ25=sQuery(id+"F0.wireOp",EDGE,"E5.2");var subQ26=sQuery(id+"F0.wireOp",EDGE,"E5.1");var subQ27=sQuery(id+"F0.wireOp",EDGE,"E5.0");var subQ28=sQuery(id+"F0.wireOp",EDGE,"E4.filletArc");var subQ29=sQuery(id+"F0.wireOp",EDGE,"E3.filletArc");var subQ30=sQuery(id+"F0.wireOp",EDGE,"E2.filletArc");var subQ31=sQuery(id+"F0.wireOp",EDGE,"E1.filletArc");var subQ32=sQuery(id+"F0.wireOp",EDGE,"E0.right");var subQ33=sQuery(id+"F0.wireOp",EDGE,"E0.left");var subQ34=sQuery(id+"F0.wireOp",EDGE,"E0.top");var subQ35=sQuery(id+"F0.wireOp",EDGE,"E0.bottom");Q0=makeQuery(id+"F3.boolean.opBoolean","MERGE",FACE,{"derivedFrom":[makeQuery(id+"F1.opExtrude","CAP_FACE",FACE,{"disambiguationData":[OSD([subQ35,subQ34,subQ33,subQ32,subQ31,subQ30,subQ29,subQ28,subQ27,subQ26,subQ25,subQ24,subQ23,subQ22,subQ21,subQ20,subQ19,subQ18,subQ17,subQ16,subQ15,subQ14,subQ13,subQ12,subQ11,subQ10,subQ9,subQ8,subQ7,subQ6,subQ5,subQ4,subQ3,subQ2,subQ1,subQ0])],"isStart":true}),makeQuery(id+"F3.opExtrude","CAP_FACE",FACE,{"disambiguationData":[OSD([subQ35,subQ34,subQ33,subQ32,subQ31,subQ30,subQ29,subQ28,subQ27,subQ26,subQ25,subQ24,subQ23,subQ22,subQ21,subQ20,subQ19,subQ18,subQ17,subQ16,subQ15,subQ14,subQ13,subQ12,subQ11,subQ10,subQ9,subQ8,subQ7,subQ6,subQ5,subQ4,subQ3,subQ2,subQ1,subQ0])],"isStart":true}),makeQuery(id+"F3.opExtrude","CAP_FACE",FACE,{"disambiguationData":[OSD([sQuery(id+"F2.wireOp",EDGE,"E37.0.0"),sQuery(id+"F2.wireOp",EDGE,"E37.0.1"),sQuery(id+"F2.wireOp",EDGE,"E37.0.2"),sQuery(id+"F2.wireOp",EDGE,"E37.0.3"),sQuery(id+"F2.wireOp",EDGE,"E37.0.4"),sQuery(id+"F2.wireOp",EDGE,"E37.0.5"),sQuery(id+"F2.wireOp",EDGE,"E37.0.6"),sQuery(id+"F2.wireOp",EDGE,"E37.0.7"),sQuery(id+"F2.wireOp",EDGE,"E37.0.8"),sQuery(id+"F2.wireOp",EDGE,"E37.0.9"),sQuery(id+"F2.wireOp",EDGE,"E37.0.10"),sQuery(id+"F2.wireOp",EDGE,"E37.0.11"),sQuery(id+"F2.wireOp",EDGE,"E37.0.12"),sQuery(id+"F2.wireOp",EDGE,"E37.0.13"),sQuery(id+"F2.wireOp",EDGE,"E37.0.14"),sQuery(id+"F2.wireOp",EDGE,"E37.0.15"),sQuery(id+"F2.wireOp",EDGE,"E37.0.16"),sQuery(id+"F2.wireOp",EDGE,"E37.0.17"),sQuery(id+"F2.wireOp",EDGE,"E37.0.18"),sQuery(id+"F2.wireOp",EDGE,"E37.0.19"),sQuery(id+"F2.wireOp",EDGE,"E37.0.20"),sQuery(id+"F2.wireOp",EDGE,"E37.0.21"),sQuery(id+"F2.wireOp",EDGE,"E37.0.22"),sQuery(id+"F2.wireOp",EDGE,"E37.0.23"),sQuery(id+"F2.wireOp",EDGE,"E37.0.24"),sQuery(id+"F2.wireOp",EDGE,"E37.0.25"),sQuery(id+"F2.wireOp",EDGE,"E37.0.26"),sQuery(id+"F2.wireOp",EDGE,"E37.0.27")])],"isStart":true})]});}
            var sketch = newSketch(context, id + "F11", { "sketchPlane" : qUnion([Q0])});
            skCircle(sketch, "E56", {"center": v(0, -15) * mm, "radius": 4 * mm});
            skSolve(sketch);
        }
        {
            var Q0;
            Q0=makeQuery(id+"F11.imprint","IMPRINT",FACE,{"disambiguationData":[TD([[makeQuery(id+"F11.imprint","IMPRINT",EDGE,{"derivedFrom":sQuery(id+"F11.wireOp",EDGE,"E56")}),1.0]])]});
            var Q1;
            Q1=makeQuery(id+"F10.opExtrude","CAP_FACE",FACE,{"disambiguationData":[OSD([sQuery(id+"F9.wireOp",EDGE,"E53")])],"isStart":false});
            extrude(context, id + "F12", {"entities" : qUnion([Q0]), "operationType" : NewBodyOperationType.REMOVE, "endBound" : BoundingType.UP_TO_SURFACE, "oppositeDirection" : true, "depth" : 25 * mm, "endBoundEntityFace" : qUnion([Q1]), "hasOffset" : true, "offsetDistance" : 5 * mm});
        }
        {
            var Q0;
            {var subQ0=sQuery(id+"F0.wireOp",EDGE,"E36.trimOffspring");var subQ1=sQuery(id+"F0.wireOp",EDGE,"E35.MirrorCS");var subQ2=sQuery(id+"F0.wireOp",EDGE,"E34.MirrorCS");var subQ3=sQuery(id+"F0.wireOp",EDGE,"E32.MirrorCS");var subQ4=sQuery(id+"F0.wireOp",EDGE,"E31.trimOffspring");var subQ5=sQuery(id+"F0.wireOp",EDGE,"E30");var subQ6=sQuery(id+"F0.wireOp",EDGE,"E29");var subQ7=sQuery(id+"F0.wireOp",EDGE,"E27");var subQ8=sQuery(id+"F0.wireOp",EDGE,"E25.MirrorCS");var subQ9=sQuery(id+"F0.wireOp",EDGE,"E23.MirrorCS");var subQ10=sQuery(id+"F0.wireOp",EDGE,"E22.MirrorCS");var subQ11=sQuery(id+"F0.wireOp",EDGE,"E21.MirrorCS");var subQ12=sQuery(id+"F0.wireOp",EDGE,"E20.MirrorCS");var subQ13=sQuery(id+"F0.wireOp",EDGE,"E18.MirrorCS");var subQ14=sQuery(id+"F0.wireOp",EDGE,"E17.MirrorCS");var subQ15=sQuery(id+"F0.wireOp",EDGE,"E16.MirrorCS");var subQ16=sQuery(id+"F0.wireOp",EDGE,"E14.MirrorCS");var subQ17=sQuery(id+"F0.wireOp",EDGE,"E13.MirrorCS");var subQ18=sQuery(id+"F0.wireOp",EDGE,"E12.MirrorCS");var subQ19=sQuery(id+"F0.wireOp",EDGE,"E8");var subQ20=sQuery(id+"F0.wireOp",EDGE,"E7");var subQ21=sQuery(id+"F0.wireOp",EDGE,"E6");var subQ22=sQuery(id+"F0.wireOp",EDGE,"E5.6");var subQ23=sQuery(id+"F0.wireOp",EDGE,"E5.5");var subQ24=sQuery(id+"F0.wireOp",EDGE,"E5.4");var subQ25=sQuery(id+"F0.wireOp",EDGE,"E5.2");var subQ26=sQuery(id+"F0.wireOp",EDGE,"E5.1");var subQ27=sQuery(id+"F0.wireOp",EDGE,"E5.0");var subQ28=sQuery(id+"F0.wireOp",EDGE,"E4.filletArc");var subQ29=sQuery(id+"F0.wireOp",EDGE,"E3.filletArc");var subQ30=sQuery(id+"F0.wireOp",EDGE,"E2.filletArc");var subQ31=sQuery(id+"F0.wireOp",EDGE,"E1.filletArc");var subQ32=sQuery(id+"F0.wireOp",EDGE,"E0.right");var subQ33=sQuery(id+"F0.wireOp",EDGE,"E0.left");var subQ34=sQuery(id+"F0.wireOp",EDGE,"E0.top");var subQ35=sQuery(id+"F0.wireOp",EDGE,"E0.bottom");Q0=makeQuery(id+"F3.boolean.opBoolean","MERGE",FACE,{"derivedFrom":[makeQuery(id+"F1.opExtrude","CAP_FACE",FACE,{"disambiguationData":[OSD([subQ35,subQ34,subQ33,subQ32,subQ31,subQ30,subQ29,subQ28,subQ27,subQ26,subQ25,subQ24,subQ23,subQ22,subQ21,subQ20,subQ19,subQ18,subQ17,subQ16,subQ15,subQ14,subQ13,subQ12,subQ11,subQ10,subQ9,subQ8,subQ7,subQ6,subQ5,subQ4,subQ3,subQ2,subQ1,subQ0])],"isStart":true}),makeQuery(id+"F3.opExtrude","CAP_FACE",FACE,{"disambiguationData":[OSD([subQ35,subQ34,subQ33,subQ32,subQ31,subQ30,subQ29,subQ28,subQ27,subQ26,subQ25,subQ24,subQ23,subQ22,subQ21,subQ20,subQ19,subQ18,subQ17,subQ16,subQ15,subQ14,subQ13,subQ12,subQ11,subQ10,subQ9,subQ8,subQ7,subQ6,subQ5,subQ4,subQ3,subQ2,subQ1,subQ0])],"isStart":true}),makeQuery(id+"F3.opExtrude","CAP_FACE",FACE,{"disambiguationData":[OSD([sQuery(id+"F2.wireOp",EDGE,"E37.0.0"),sQuery(id+"F2.wireOp",EDGE,"E37.0.1"),sQuery(id+"F2.wireOp",EDGE,"E37.0.2"),sQuery(id+"F2.wireOp",EDGE,"E37.0.3"),sQuery(id+"F2.wireOp",EDGE,"E37.0.4"),sQuery(id+"F2.wireOp",EDGE,"E37.0.5"),sQuery(id+"F2.wireOp",EDGE,"E37.0.6"),sQuery(id+"F2.wireOp",EDGE,"E37.0.7"),sQuery(id+"F2.wireOp",EDGE,"E37.0.8"),sQuery(id+"F2.wireOp",EDGE,"E37.0.9"),sQuery(id+"F2.wireOp",EDGE,"E37.0.10"),sQuery(id+"F2.wireOp",EDGE,"E37.0.11"),sQuery(id+"F2.wireOp",EDGE,"E37.0.12"),sQuery(id+"F2.wireOp",EDGE,"E37.0.13"),sQuery(id+"F2.wireOp",EDGE,"E37.0.14"),sQuery(id+"F2.wireOp",EDGE,"E37.0.15"),sQuery(id+"F2.wireOp",EDGE,"E37.0.16"),sQuery(id+"F2.wireOp",EDGE,"E37.0.17"),sQuery(id+"F2.wireOp",EDGE,"E37.0.18"),sQuery(id+"F2.wireOp",EDGE,"E37.0.19"),sQuery(id+"F2.wireOp",EDGE,"E37.0.20"),sQuery(id+"F2.wireOp",EDGE,"E37.0.21"),sQuery(id+"F2.wireOp",EDGE,"E37.0.22"),sQuery(id+"F2.wireOp",EDGE,"E37.0.23"),sQuery(id+"F2.wireOp",EDGE,"E37.0.24"),sQuery(id+"F2.wireOp",EDGE,"E37.0.25"),sQuery(id+"F2.wireOp",EDGE,"E37.0.26"),sQuery(id+"F2.wireOp",EDGE,"E37.0.27")])],"isStart":true})]});}
            var sketch = newSketch(context, id + "F13", { "sketchPlane" : qUnion([Q0])});
            skPoint(sketch, "E57", {"position": v(0, 15) * mm});
            skSolve(sketch);
        }
        {
            var Q0;
            Q0=sQuery(id+"F13.wireOp",VERTEX,"E57");
            var Q1;
            Q1=makeQuery(id+"F1.opExtrude","SWEPT_BODY",BODY,{"disambiguationData":[OSD([sQuery(id+"F0.wireOp",EDGE,"E0.bottom"),sQuery(id+"F0.wireOp",EDGE,"E0.top"),sQuery(id+"F0.wireOp",EDGE,"E0.left"),sQuery(id+"F0.wireOp",EDGE,"E0.right"),sQuery(id+"F0.wireOp",EDGE,"E1.filletArc"),sQuery(id+"F0.wireOp",EDGE,"E2.filletArc"),sQuery(id+"F0.wireOp",EDGE,"E3.filletArc"),sQuery(id+"F0.wireOp",EDGE,"E4.filletArc"),sQuery(id+"F0.wireOp",EDGE,"E5.0"),sQuery(id+"F0.wireOp",EDGE,"E5.1"),sQuery(id+"F0.wireOp",EDGE,"E5.2"),sQuery(id+"F0.wireOp",EDGE,"E5.4"),sQuery(id+"F0.wireOp",EDGE,"E5.5"),sQuery(id+"F0.wireOp",EDGE,"E5.6"),sQuery(id+"F0.wireOp",EDGE,"E6"),sQuery(id+"F0.wireOp",EDGE,"E7"),sQuery(id+"F0.wireOp",EDGE,"E8"),sQuery(id+"F0.wireOp",EDGE,"E12.MirrorCS"),sQuery(id+"F0.wireOp",EDGE,"E13.MirrorCS"),sQuery(id+"F0.wireOp",EDGE,"E14.MirrorCS"),sQuery(id+"F0.wireOp",EDGE,"E16.MirrorCS"),sQuery(id+"F0.wireOp",EDGE,"E17.MirrorCS"),sQuery(id+"F0.wireOp",EDGE,"E18.MirrorCS"),sQuery(id+"F0.wireOp",EDGE,"E20.MirrorCS"),sQuery(id+"F0.wireOp",EDGE,"E21.MirrorCS"),sQuery(id+"F0.wireOp",EDGE,"E22.MirrorCS"),sQuery(id+"F0.wireOp",EDGE,"E23.MirrorCS"),sQuery(id+"F0.wireOp",EDGE,"E25.MirrorCS"),sQuery(id+"F0.wireOp",EDGE,"E27"),sQuery(id+"F0.wireOp",EDGE,"E29"),sQuery(id+"F0.wireOp",EDGE,"E30"),sQuery(id+"F0.wireOp",EDGE,"E31.trimOffspring"),sQuery(id+"F0.wireOp",EDGE,"E32.MirrorCS"),sQuery(id+"F0.wireOp",EDGE,"E34.MirrorCS"),sQuery(id+"F0.wireOp",EDGE,"E35.MirrorCS"),sQuery(id+"F0.wireOp",EDGE,"E36.trimOffspring")])]});
            hole(context, id + "F14", {"style" : HoleStyle.SIMPLE, "endStyle" : HoleEndStyle.BLIND, "standardTappedOrClearance" : lookupTablePath({ "standard" : "ISO", "fit" : "Close", "size" : "M12", "type" : "Clearance" }), "standardBlindInLast" : lookupTablePath({ "fit" : "Close", "standard" : "ISO", "size" : "M12", "type" : "Clearance" }), "holeDiameter" : 12.6 * mm, "holeDepth" : 40.6 * mm, "isTappedThrough" : true, "tappedDepth" : 37.6 * mm, "tapClearance" : 3, "locations" : qUnion([Q0]), "scope" : qUnion([Q1])});
        }
        {
            var Q0;
            {var subQ0=sQuery(id+"F0.wireOp",EDGE,"E36.trimOffspring");var subQ1=sQuery(id+"F0.wireOp",EDGE,"E35.MirrorCS");var subQ2=sQuery(id+"F0.wireOp",EDGE,"E34.MirrorCS");var subQ3=sQuery(id+"F0.wireOp",EDGE,"E32.MirrorCS");var subQ4=sQuery(id+"F0.wireOp",EDGE,"E31.trimOffspring");var subQ5=sQuery(id+"F0.wireOp",EDGE,"E30");var subQ6=sQuery(id+"F0.wireOp",EDGE,"E29");var subQ7=sQuery(id+"F0.wireOp",EDGE,"E27");var subQ8=sQuery(id+"F0.wireOp",EDGE,"E25.MirrorCS");var subQ9=sQuery(id+"F0.wireOp",EDGE,"E23.MirrorCS");var subQ10=sQuery(id+"F0.wireOp",EDGE,"E22.MirrorCS");var subQ11=sQuery(id+"F0.wireOp",EDGE,"E21.MirrorCS");var subQ12=sQuery(id+"F0.wireOp",EDGE,"E20.MirrorCS");var subQ13=sQuery(id+"F0.wireOp",EDGE,"E18.MirrorCS");var subQ14=sQuery(id+"F0.wireOp",EDGE,"E17.MirrorCS");var subQ15=sQuery(id+"F0.wireOp",EDGE,"E16.MirrorCS");var subQ16=sQuery(id+"F0.wireOp",EDGE,"E14.MirrorCS");var subQ17=sQuery(id+"F0.wireOp",EDGE,"E13.MirrorCS");var subQ18=sQuery(id+"F0.wireOp",EDGE,"E12.MirrorCS");var subQ19=sQuery(id+"F0.wireOp",EDGE,"E8");var subQ20=sQuery(id+"F0.wireOp",EDGE,"E7");var subQ21=sQuery(id+"F0.wireOp",EDGE,"E6");var subQ22=sQuery(id+"F0.wireOp",EDGE,"E5.6");var subQ23=sQuery(id+"F0.wireOp",EDGE,"E5.5");var subQ24=sQuery(id+"F0.wireOp",EDGE,"E5.4");var subQ25=sQuery(id+"F0.wireOp",EDGE,"E5.2");var subQ26=sQuery(id+"F0.wireOp",EDGE,"E5.1");var subQ27=sQuery(id+"F0.wireOp",EDGE,"E5.0");var subQ28=sQuery(id+"F0.wireOp",EDGE,"E4.filletArc");var subQ29=sQuery(id+"F0.wireOp",EDGE,"E3.filletArc");var subQ30=sQuery(id+"F0.wireOp",EDGE,"E2.filletArc");var subQ31=sQuery(id+"F0.wireOp",EDGE,"E1.filletArc");var subQ32=sQuery(id+"F0.wireOp",EDGE,"E0.right");var subQ33=sQuery(id+"F0.wireOp",EDGE,"E0.left");var subQ34=sQuery(id+"F0.wireOp",EDGE,"E0.top");var subQ35=sQuery(id+"F0.wireOp",EDGE,"E0.bottom");Q0=makeQuery(id+"F3.boolean.opBoolean","MERGE",FACE,{"derivedFrom":[makeQuery(id+"F1.opExtrude","CAP_FACE",FACE,{"disambiguationData":[OSD([subQ35,subQ34,subQ33,subQ32,subQ31,subQ30,subQ29,subQ28,subQ27,subQ26,subQ25,subQ24,subQ23,subQ22,subQ21,subQ20,subQ19,subQ18,subQ17,subQ16,subQ15,subQ14,subQ13,subQ12,subQ11,subQ10,subQ9,subQ8,subQ7,subQ6,subQ5,subQ4,subQ3,subQ2,subQ1,subQ0])],"isStart":true}),makeQuery(id+"F3.opExtrude","CAP_FACE",FACE,{"disambiguationData":[OSD([subQ35,subQ34,subQ33,subQ32,subQ31,subQ30,subQ29,subQ28,subQ27,subQ26,subQ25,subQ24,subQ23,subQ22,subQ21,subQ20,subQ19,subQ18,subQ17,subQ16,subQ15,subQ14,subQ13,subQ12,subQ11,subQ10,subQ9,subQ8,subQ7,subQ6,subQ5,subQ4,subQ3,subQ2,subQ1,subQ0])],"isStart":true}),makeQuery(id+"F3.opExtrude","CAP_FACE",FACE,{"disambiguationData":[OSD([sQuery(id+"F2.wireOp",EDGE,"E37.0.0"),sQuery(id+"F2.wireOp",EDGE,"E37.0.1"),sQuery(id+"F2.wireOp",EDGE,"E37.0.2"),sQuery(id+"F2.wireOp",EDGE,"E37.0.3"),sQuery(id+"F2.wireOp",EDGE,"E37.0.4"),sQuery(id+"F2.wireOp",EDGE,"E37.0.5"),sQuery(id+"F2.wireOp",EDGE,"E37.0.6"),sQuery(id+"F2.wireOp",EDGE,"E37.0.7"),sQuery(id+"F2.wireOp",EDGE,"E37.0.8"),sQuery(id+"F2.wireOp",EDGE,"E37.0.9"),sQuery(id+"F2.wireOp",EDGE,"E37.0.10"),sQuery(id+"F2.wireOp",EDGE,"E37.0.11"),sQuery(id+"F2.wireOp",EDGE,"E37.0.12"),sQuery(id+"F2.wireOp",EDGE,"E37.0.13"),sQuery(id+"F2.wireOp",EDGE,"E37.0.14"),sQuery(id+"F2.wireOp",EDGE,"E37.0.15"),sQuery(id+"F2.wireOp",EDGE,"E37.0.16"),sQuery(id+"F2.wireOp",EDGE,"E37.0.17"),sQuery(id+"F2.wireOp",EDGE,"E37.0.18"),sQuery(id+"F2.wireOp",EDGE,"E37.0.19"),sQuery(id+"F2.wireOp",EDGE,"E37.0.20"),sQuery(id+"F2.wireOp",EDGE,"E37.0.21"),sQuery(id+"F2.wireOp",EDGE,"E37.0.22"),sQuery(id+"F2.wireOp",EDGE,"E37.0.23"),sQuery(id+"F2.wireOp",EDGE,"E37.0.24"),sQuery(id+"F2.wireOp",EDGE,"E37.0.25"),sQuery(id+"F2.wireOp",EDGE,"E37.0.26"),sQuery(id+"F2.wireOp",EDGE,"E37.0.27")])],"isStart":true})]});}
            var sketch = newSketch(context, id + "F15", { "sketchPlane" : qUnion([Q0])});
            skCircle(sketch, "E58", {"center": v(0, 15) * mm, "radius": 9 * mm});
            skCircle(sketch, "E59", {"center": v(0, 15) * mm, "radius": 12.5 * mm});
            skSolve(sketch);
        }
        {
            var Q0;
            Q0 = qSketchRegion(id + "F15", true);
            extrude(context, id + "F16", {"entities" : qUnion([Q0]), "operationType" : NewBodyOperationType.REMOVE, "oppositeDirection" : true, "depth" : 2.1 * mm, "offsetDistance" : 25 * mm});
        }
        {
            var Q0;
            Q0=makeQuery(id+"F16.boolean.opBoolean","COPY",FACE,{"derivedFrom":makeQuery(id+"F16.opExtrude","CAP_FACE",FACE,{"disambiguationData":[OSD([sQuery(id+"F15.wireOp",EDGE,"E58"),sQuery(id+"F15.wireOp",EDGE,"E59")])],"isStart":false})});
            fillet(context, id + "F17", {"entities" : qUnion([Q0]), "radius" : 0.5 * mm, "tangentPropagation" : true, "allowEdgeOverflow" : false});
        }
    });
